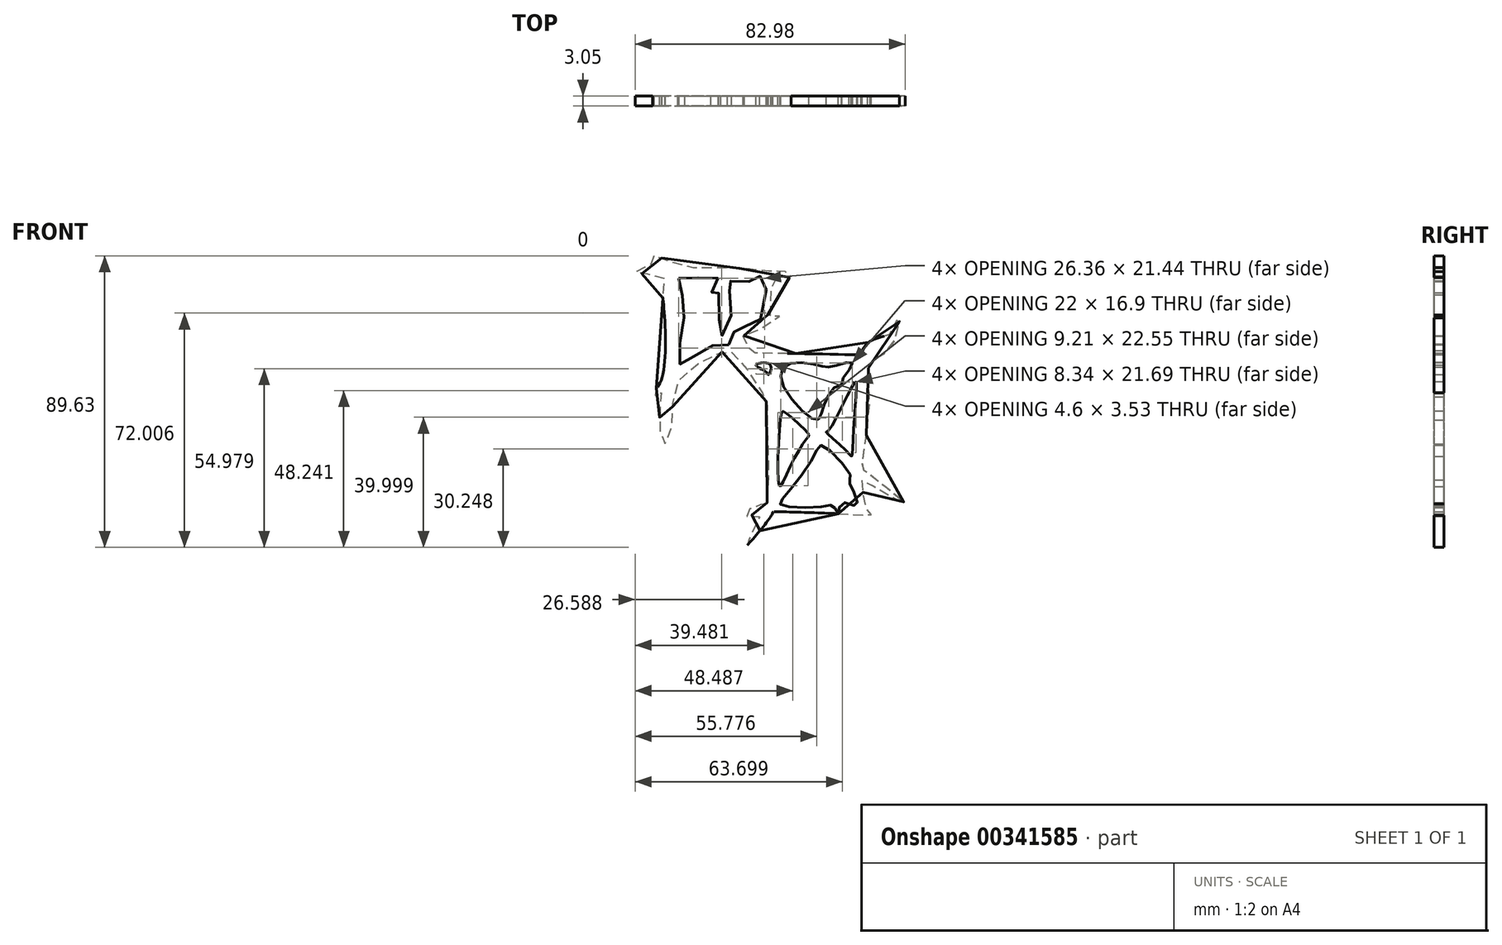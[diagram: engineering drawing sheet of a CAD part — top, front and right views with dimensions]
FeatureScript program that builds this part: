
annotation { "Feature Type Name" : "Feature", "Feature Type Description" : "" }
export const myFeature = defineFeature(function(context is Context, id is Id, definition is map)
    precondition{}
    {
        {
            var Q0;
            Q0=qCreatedBy(makeId("Front.planeOp"),FACE);
            var sketch = newSketch(context, id + "F0", { "sketchPlane" : qUnion([Q0])});
            skFitSpline(sketch, "E0", {"points": [v(-25.73, 42.58) * mm, v(-17.89, 41.56) * mm, v(-16.62, 39.29) * mm, v(-17.38, 37.01) * mm, v(-17.13, 33.98) * mm, v(-17.63, 9.7) * mm, v(-19.91, 5.65) * mm, v(-18.9, 4.38) * mm, v(-17.63, 5.65) * mm, v(-17.89, 4.13) * mm, v(-17.13, -10.03) * mm, v(-14.6, -5.73) * mm, v(-12.58, 8.94) * mm, v(0, 17.79) * mm, v(4.37, 17.79) * mm, v(14.23, 3.88) * mm, v(14.74, 0) * mm, v(14.49, -29.26) * mm, v(13.22, -29) * mm, v(10.95, -29) * mm, v(7.91, -32.3) * mm, v(12.46, -32.04) * mm, v(7.91, -41.9) * mm, v(16.51, -31.28) * mm, v(16.51, -31.03) * mm, v(41.55, -31.79) * mm, v(46.86, -31.79) * mm, v(45.1, -29.51) * mm, v(44.08, -21.42) * mm, v(44.08, -21.16) * mm, v(57.23, -28.5) * mm, v(43.83, -17.62) * mm, v(43.83, -17.12) * mm, v(46.36, 5.65) * mm, v(46.1, 5.4) * mm, v(45.85, 12.22) * mm, v(47.37, 15.76) * mm, v(53.19, 20.06) * mm, v(55.2, 28.66) * mm, v(52.17, 23.1) * mm, v(51.92, 23.1) * mm, v(45.6, 20.82) * mm, v(43.83, 17.54) * mm, v(42.82, 17.28) * mm, v(10.7, 17.79) * mm, v(9.93, 18.04) * mm, v(7.4, 22.85) * mm, v(8.67, 23.35) * mm, v(18.79, 29.42) * mm, v(15.25, 29.17) * mm, v(16.51, 33.98) * mm, v(16.51, 40.55) * mm, v(22.08, 41.31) * mm, v(21.57, 42.58) * mm, v(18.53, 42.83) * mm, v(2.35, 44.1) * mm, v(-11.31, 44.6) * mm, v(-20.16, 47.63) * mm, v(-20.67, 45.36) * mm, v(-25.73, 42.58) * mm]});
            skFitSpline(sketch, "E1", {"points": [v(-12.32, 40.8) * mm, v(-10.8, 34.23) * mm, v(-11.56, 23.86) * mm, v(-11.82, 14.25) * mm, v(-9.54, 15.51) * mm, v(0, 20.57) * mm, v(3.36, 20.57) * mm, v(4.88, 24.87) * mm, v(7.4, 25.88) * mm, v(12.72, 28.16) * mm, v(13.73, 41.31) * mm, v(11.7, 40.8) * mm, v(8.67, 39.8) * mm, v(2.85, 39.8) * mm, v(3.1, 37.52) * mm, v(2.85, 25.63) * mm, v(0, 23.35) * mm, v(0, 36.25) * mm, v(-2.46, 35.75) * mm, v(0, 40.3) * mm, v(-3.98, 40.8) * mm, v(-12.32, 40.8) * mm]});
            skFitSpline(sketch, "E2", {"points": [v(11.45, 14.25) * mm, v(15.75, 14.25) * mm, v(15.25, 11.21) * mm, v(14.49, 11.97) * mm, v(11.45, 14.25) * mm]});
            skFitSpline(sketch, "E3", {"points": [v(41.05, 14.75) * mm, v(37.76, 9.19) * mm, v(37.76, 8.18) * mm, v(35.73, 7.42) * mm, v(31.69, 0) * mm, v(29.92, -2.7) * mm, v(19.8, 7.67) * mm, v(20.81, 14.25) * mm, v(30.93, 14) * mm, v(34.98, 13.74) * mm, v(41.05, 14.75) * mm]});
            skFitSpline(sketch, "E4", {"points": [v(41.8, 8.94) * mm, v(41.8, 1.35) * mm, v(40.8, -13.83) * mm, v(40.03, -13.07) * mm, v(32.95, -6.5) * mm, v(33.46, -6.24) * mm, v(41.8, 8.94) * mm]});
            skFitSpline(sketch, "E5", {"points": [v(18.53, -22.93) * mm, v(19.3, -0.42) * mm, v(20.05, -0.17) * mm, v(27.64, -7.25) * mm, v(27.13, -8.26) * mm, v(20.81, -19.4) * mm, v(18.53, -22.93) * mm]});
            skFitSpline(sketch, "E6", {"points": [v(31.69, -10.54) * mm, v(40.54, -20.15) * mm, v(40.03, -21.42) * mm, v(40.8, -23.44) * mm, v(42.31, -29) * mm, v(37.76, -28.25) * mm, v(36.68, -31.54) * mm, v(35.23, -29.26) * mm, v(32.45, -29.26) * mm, v(19.04, -28.75) * mm, v(19.55, -26.98) * mm, v(29.41, -13.58) * mm, v(31.69, -10.54) * mm]});
            skSolve(sketch);
        }
        {
            var Q0;
            Q0=makeQuery(id+"F0.imprint","IMPRINT",FACE,{"disambiguationData":[TD([[makeQuery(id+"F0.imprint","IMPRINT",EDGE,{"derivedFrom":sQuery(id+"F0.wireOp",EDGE,"E1")}),-1.0]])]});
            extrude(context, id + "F1", {"entities" : qUnion([Q0]), "depth" : 3.05 * mm});
        }
    });
